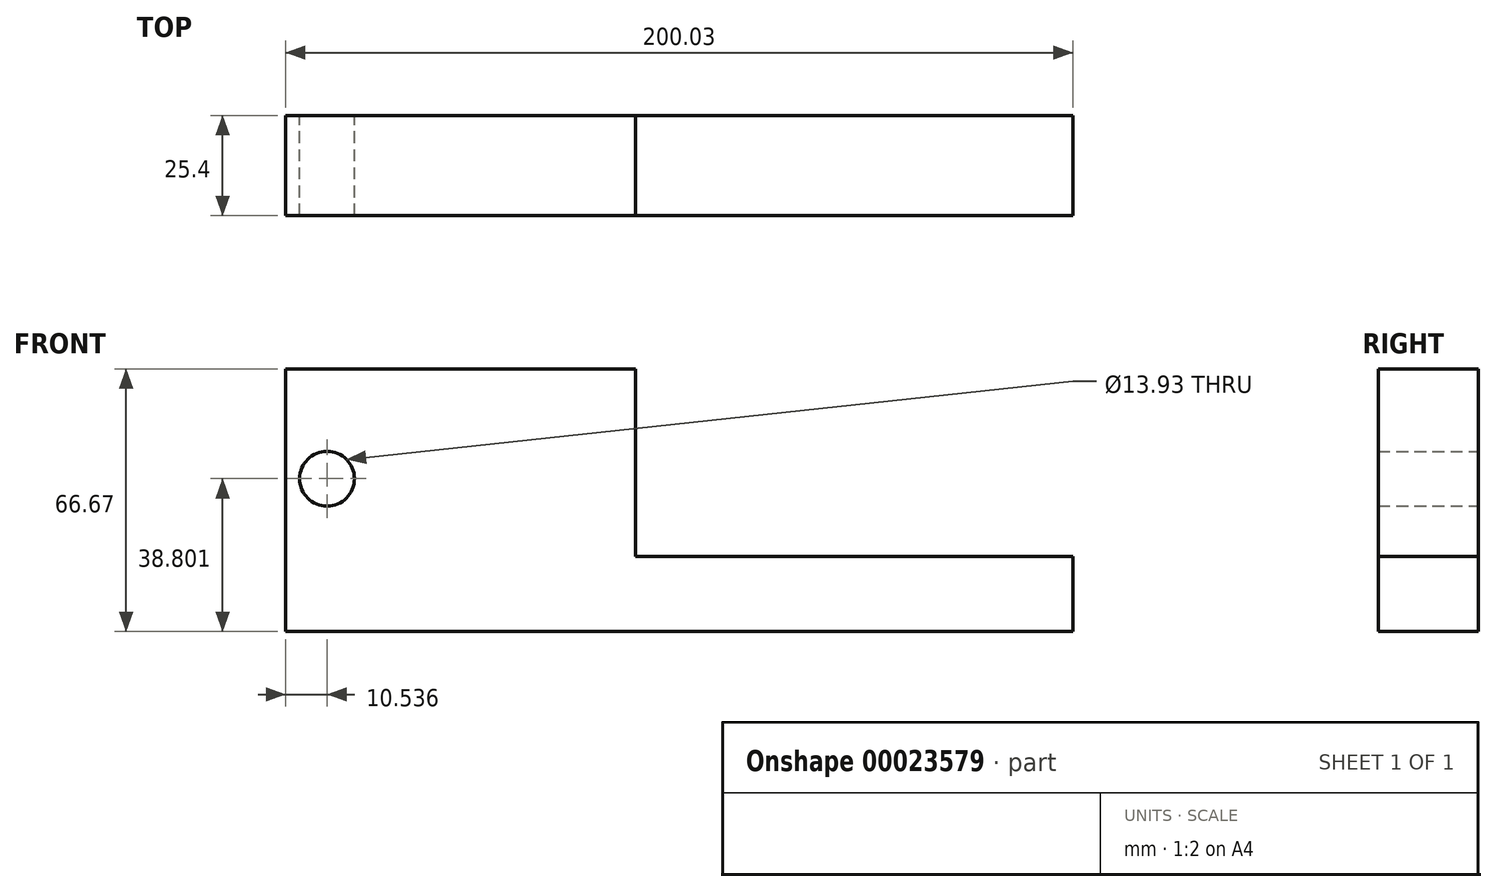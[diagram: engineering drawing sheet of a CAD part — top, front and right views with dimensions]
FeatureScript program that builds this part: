
annotation { "Feature Type Name" : "Feature", "Feature Type Description" : "" }
export const myFeature = defineFeature(function(context is Context, id is Id, definition is map)
    precondition{}
    {
        {
            var Q0;
            Q0=qCreatedBy(makeId("Front.planeOp"),FACE);
            var sketch = newSketch(context, id + "F0", { "sketchPlane" : qUnion([Q0])});
            skLineSegment(sketch, "E0.bottom", {"start": v(0, 0) * mm, "end": v(200.02, 0) * mm});
            skLineSegment(sketch, "E0.top", {"start": v(0, -19.05) * mm, "end": v(200.03, -19.05) * mm});
            skLineSegment(sketch, "E0.left", {"start": v(0, 0) * mm, "end": v(0, -19.05) * mm});
            skLineSegment(sketch, "E0.right", {"start": v(200.02, 0) * mm, "end": v(200.02, -19.05) * mm});
            skLineSegment(sketch, "E1.bottom", {"start": v(0, -19.05) * mm, "end": v(88.9, -19.05) * mm});
            skLineSegment(sketch, "E1.top", {"start": v(0, 47.62) * mm, "end": v(88.9, 47.62) * mm});
            skLineSegment(sketch, "E1.left", {"start": v(0, -19.05) * mm, "end": v(0, 47.62) * mm});
            skLineSegment(sketch, "E1.right", {"start": v(88.9, -19.05) * mm, "end": v(88.9, 47.63) * mm});
            skLineSegment(sketch, "E2", {"start": v(9.52, 47.63) * mm, "end": v(25.4, 31.75) * mm});
            skLineSegment(sketch, "E3", {"start": v(25.4, 31.75) * mm, "end": v(25.4, 0) * mm});
            skLineSegment(sketch, "E4", {"start": v(38.1, 0) * mm, "end": v(38.1, 6.35) * mm});
            skLineSegment(sketch, "E5", {"start": v(38.1, 6.35) * mm, "end": v(79.38, 47.63) * mm});
            skPoint(sketch, "E6.orphan", {"position": v(25.4, 0) * mm});
            skPoint(sketch, "E7.orphan", {"position": v(38.1, -25.4) * mm});
            skCircle(sketch, "E8", {"center": v(10.54, 19.75) * mm, "radius": 6.97 * mm});
            skSolve(sketch);
        }
        {
            var Q0;
            Q0 = qSketchRegion(id + "F0", true);
            extrude(context, id + "F1", {"entities" : qUnion([Q0]), "depth" : 25.4 * mm});
        }
    });
